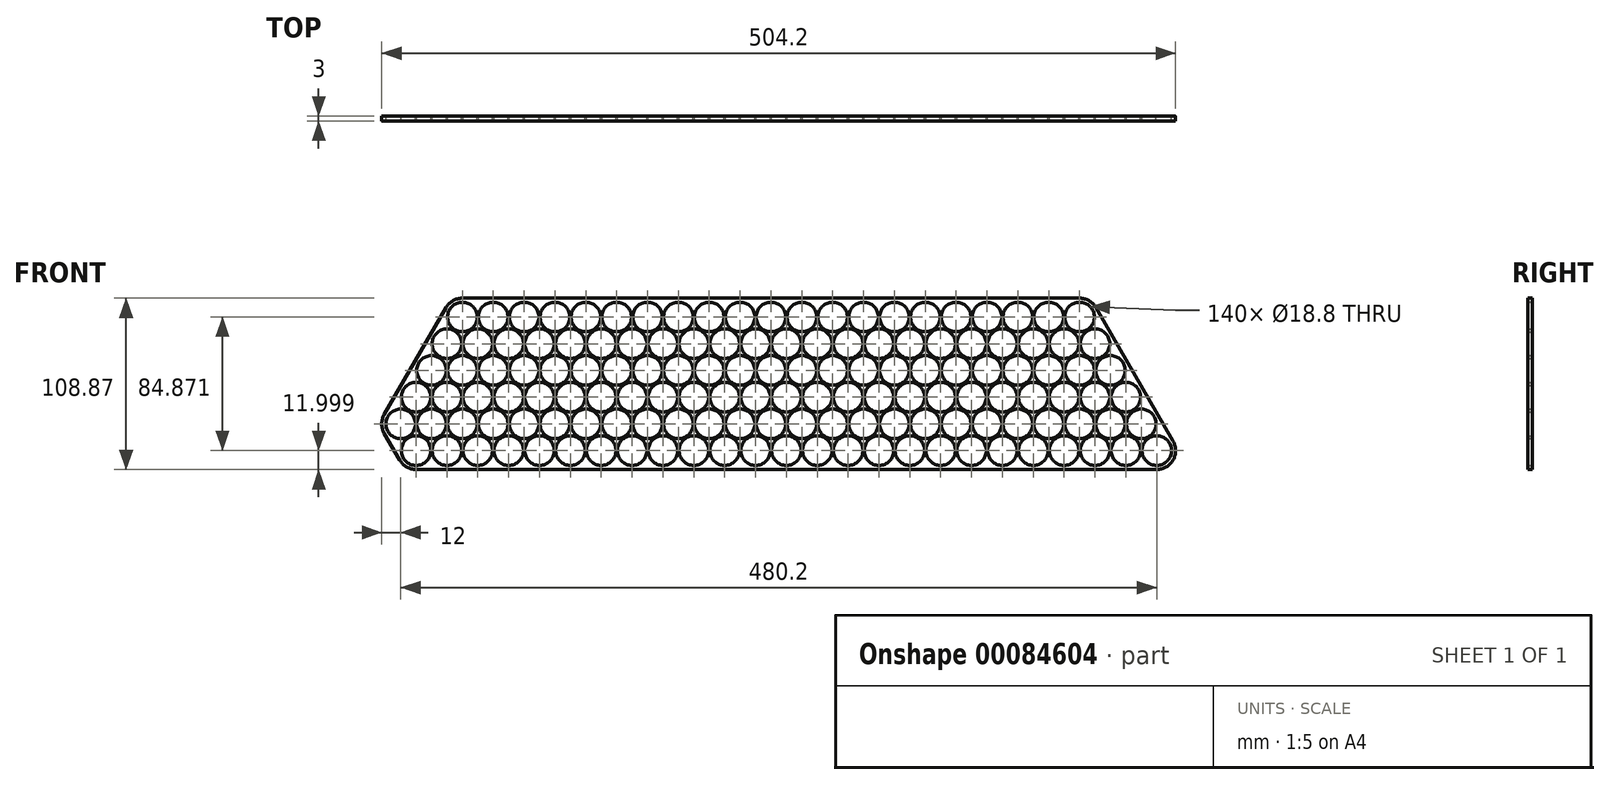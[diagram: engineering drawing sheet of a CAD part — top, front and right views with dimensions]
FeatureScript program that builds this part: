
annotation { "Feature Type Name" : "Feature", "Feature Type Description" : "" }
export const myFeature = defineFeature(function(context is Context, id is Id, definition is map)
    precondition{}
    {
        {
            var Q0;
            Q0=qCreatedBy(makeId("Front.planeOp"),FACE);
            var sketch = newSketch(context, id + "F0", { "sketchPlane" : qUnion([Q0]) });
            skLineSegment(sketch, "E0", {"start": v(0, 0) * mm, "end": v(79.44, 0) * mm, "construction": true});
            skLineSegment(sketch, "E1", {"start": v(0, 0) * mm, "end": v(43.4, -75.16) * mm, "construction": true});
            skCircle(sketch, "E2", {"center": v(0, 0) * mm, "radius": 9.4 * mm});
            skCircle(sketch, "E3.1.0.0", {"center": v(19.6, 0) * mm, "radius": 9.4 * mm});
            skCircle(sketch, "E3.2.0.0", {"center": v(39.2, 0) * mm, "radius": 9.4 * mm});
            skCircle(sketch, "E3.3.0.0", {"center": v(58.8, 0) * mm, "radius": 9.4 * mm});
            skCircle(sketch, "E3.4.0.0", {"center": v(78.4, 0) * mm, "radius": 9.4 * mm});
            skCircle(sketch, "E3.5.0.0", {"center": v(98, 0) * mm, "radius": 9.4 * mm});
            skCircle(sketch, "E3.6.0.0", {"center": v(117.6, 0) * mm, "radius": 9.4 * mm});
            skCircle(sketch, "E3.7.0.0", {"center": v(137.2, 0) * mm, "radius": 9.4 * mm});
            skCircle(sketch, "E3.8.0.0", {"center": v(156.8, 0) * mm, "radius": 9.4 * mm});
            skCircle(sketch, "E3.9.0.0", {"center": v(176.4, 0) * mm, "radius": 9.4 * mm});
            skCircle(sketch, "E3.10.0.0", {"center": v(196, 0) * mm, "radius": 9.4 * mm});
            skCircle(sketch, "E3.11.0.0", {"center": v(215.6, 0) * mm, "radius": 9.4 * mm});
            skCircle(sketch, "E3.12.0.0", {"center": v(235.2, 0) * mm, "radius": 9.4 * mm});
            skCircle(sketch, "E3.13.0.0", {"center": v(254.8, 0) * mm, "radius": 9.4 * mm});
            skCircle(sketch, "E3.14.0.0", {"center": v(274.4, 0) * mm, "radius": 9.4 * mm});
            skCircle(sketch, "E3.15.0.0", {"center": v(294, 0) * mm, "radius": 9.4 * mm});
            skCircle(sketch, "E3.16.0.0", {"center": v(313.6, 0) * mm, "radius": 9.4 * mm});
            skCircle(sketch, "E3.17.0.0", {"center": v(333.2, 0) * mm, "radius": 9.4 * mm});
            skCircle(sketch, "E3.18.0.0", {"center": v(352.8, 0) * mm, "radius": 9.4 * mm});
            skCircle(sketch, "E3.19.0.0", {"center": v(372.4, 0) * mm, "radius": 9.4 * mm});
            skLineSegment(sketch, "E3.direction1", {"start": v(0, 0) * mm, "end": v(19.6, 0) * mm, "construction": true});
            skCircle(sketch, "E4.1.0.0", {"center": v(9.8, -16.97) * mm, "radius": 9.4 * mm});
            skCircle(sketch, "E4.2.0.0", {"center": v(19.6, -33.95) * mm, "radius": 9.4 * mm});
            skCircle(sketch, "E4.3.0.0", {"center": v(29.4, -50.92) * mm, "radius": 9.4 * mm});
            skCircle(sketch, "E4.4.0.0", {"center": v(39.2, -67.9) * mm, "radius": 9.4 * mm});
            skCircle(sketch, "E4.5.0.0", {"center": v(49, -84.87) * mm, "radius": 9.4 * mm});
            skLineSegment(sketch, "E4.direction1", {"start": v(0, 0) * mm, "end": v(9.8, -16.97) * mm, "construction": true});
            skCircle(sketch, "E5.1.0.0", {"center": v(29.4, -16.97) * mm, "radius": 9.4 * mm});
            skCircle(sketch, "E5.1.0.1", {"center": v(39.2, -33.95) * mm, "radius": 9.4 * mm});
            skCircle(sketch, "E5.1.0.2", {"center": v(49, -50.92) * mm, "radius": 9.4 * mm});
            skCircle(sketch, "E5.1.0.3", {"center": v(58.8, -67.9) * mm, "radius": 9.4 * mm});
            skCircle(sketch, "E5.1.0.4", {"center": v(68.6, -84.87) * mm, "radius": 9.4 * mm});
            skCircle(sketch, "E5.2.0.0", {"center": v(49, -16.97) * mm, "radius": 9.4 * mm});
            skCircle(sketch, "E5.2.0.1", {"center": v(58.8, -33.95) * mm, "radius": 9.4 * mm});
            skCircle(sketch, "E5.2.0.2", {"center": v(68.6, -50.92) * mm, "radius": 9.4 * mm});
            skCircle(sketch, "E5.2.0.3", {"center": v(78.4, -67.9) * mm, "radius": 9.4 * mm});
            skCircle(sketch, "E5.2.0.4", {"center": v(88.2, -84.87) * mm, "radius": 9.4 * mm});
            skCircle(sketch, "E5.3.0.0", {"center": v(68.6, -16.97) * mm, "radius": 9.4 * mm});
            skCircle(sketch, "E5.3.0.1", {"center": v(78.4, -33.95) * mm, "radius": 9.4 * mm});
            skCircle(sketch, "E5.3.0.2", {"center": v(88.2, -50.92) * mm, "radius": 9.4 * mm});
            skCircle(sketch, "E5.3.0.3", {"center": v(98, -67.9) * mm, "radius": 9.4 * mm});
            skCircle(sketch, "E5.3.0.4", {"center": v(107.8, -84.87) * mm, "radius": 9.4 * mm});
            skCircle(sketch, "E5.4.0.0", {"center": v(88.2, -16.97) * mm, "radius": 9.4 * mm});
            skCircle(sketch, "E5.4.0.1", {"center": v(98, -33.95) * mm, "radius": 9.4 * mm});
            skCircle(sketch, "E5.4.0.2", {"center": v(107.8, -50.92) * mm, "radius": 9.4 * mm});
            skCircle(sketch, "E5.4.0.3", {"center": v(117.6, -67.9) * mm, "radius": 9.4 * mm});
            skCircle(sketch, "E5.4.0.4", {"center": v(127.4, -84.87) * mm, "radius": 9.4 * mm});
            skCircle(sketch, "E5.5.0.0", {"center": v(107.8, -16.97) * mm, "radius": 9.4 * mm});
            skCircle(sketch, "E5.5.0.1", {"center": v(117.6, -33.95) * mm, "radius": 9.4 * mm});
            skCircle(sketch, "E5.5.0.2", {"center": v(127.4, -50.92) * mm, "radius": 9.4 * mm});
            skCircle(sketch, "E5.5.0.3", {"center": v(137.2, -67.9) * mm, "radius": 9.4 * mm});
            skCircle(sketch, "E5.5.0.4", {"center": v(147, -84.87) * mm, "radius": 9.4 * mm});
            skCircle(sketch, "E5.6.0.0", {"center": v(127.4, -16.97) * mm, "radius": 9.4 * mm});
            skCircle(sketch, "E5.6.0.1", {"center": v(137.2, -33.95) * mm, "radius": 9.4 * mm});
            skCircle(sketch, "E5.6.0.2", {"center": v(147, -50.92) * mm, "radius": 9.4 * mm});
            skCircle(sketch, "E5.6.0.3", {"center": v(156.8, -67.9) * mm, "radius": 9.4 * mm});
            skCircle(sketch, "E5.6.0.4", {"center": v(166.6, -84.87) * mm, "radius": 9.4 * mm});
            skCircle(sketch, "E5.7.0.0", {"center": v(147, -16.97) * mm, "radius": 9.4 * mm});
            skCircle(sketch, "E5.7.0.1", {"center": v(156.8, -33.95) * mm, "radius": 9.4 * mm});
            skCircle(sketch, "E5.7.0.2", {"center": v(166.6, -50.92) * mm, "radius": 9.4 * mm});
            skCircle(sketch, "E5.7.0.3", {"center": v(176.4, -67.9) * mm, "radius": 9.4 * mm});
            skCircle(sketch, "E5.7.0.4", {"center": v(186.2, -84.87) * mm, "radius": 9.4 * mm});
            skCircle(sketch, "E5.8.0.0", {"center": v(166.6, -16.97) * mm, "radius": 9.4 * mm});
            skCircle(sketch, "E5.8.0.1", {"center": v(176.4, -33.95) * mm, "radius": 9.4 * mm});
            skCircle(sketch, "E5.8.0.2", {"center": v(186.2, -50.92) * mm, "radius": 9.4 * mm});
            skCircle(sketch, "E5.8.0.3", {"center": v(196, -67.9) * mm, "radius": 9.4 * mm});
            skCircle(sketch, "E5.8.0.4", {"center": v(205.8, -84.87) * mm, "radius": 9.4 * mm});
            skCircle(sketch, "E5.9.0.0", {"center": v(186.2, -16.97) * mm, "radius": 9.4 * mm});
            skCircle(sketch, "E5.9.0.1", {"center": v(196, -33.95) * mm, "radius": 9.4 * mm});
            skCircle(sketch, "E5.9.0.2", {"center": v(205.8, -50.92) * mm, "radius": 9.4 * mm});
            skCircle(sketch, "E5.9.0.3", {"center": v(215.6, -67.9) * mm, "radius": 9.4 * mm});
            skCircle(sketch, "E5.9.0.4", {"center": v(225.4, -84.87) * mm, "radius": 9.4 * mm});
            skCircle(sketch, "E5.10.0.0", {"center": v(205.8, -16.97) * mm, "radius": 9.4 * mm});
            skCircle(sketch, "E5.10.0.1", {"center": v(215.6, -33.95) * mm, "radius": 9.4 * mm});
            skCircle(sketch, "E5.10.0.2", {"center": v(225.4, -50.92) * mm, "radius": 9.4 * mm});
            skCircle(sketch, "E5.10.0.3", {"center": v(235.2, -67.9) * mm, "radius": 9.4 * mm});
            skCircle(sketch, "E5.10.0.4", {"center": v(245, -84.87) * mm, "radius": 9.4 * mm});
            skCircle(sketch, "E5.11.0.0", {"center": v(225.4, -16.97) * mm, "radius": 9.4 * mm});
            skCircle(sketch, "E5.11.0.1", {"center": v(235.2, -33.95) * mm, "radius": 9.4 * mm});
            skCircle(sketch, "E5.11.0.2", {"center": v(245, -50.92) * mm, "radius": 9.4 * mm});
            skCircle(sketch, "E5.11.0.3", {"center": v(254.8, -67.9) * mm, "radius": 9.4 * mm});
            skCircle(sketch, "E5.11.0.4", {"center": v(264.6, -84.87) * mm, "radius": 9.4 * mm});
            skCircle(sketch, "E5.12.0.0", {"center": v(245, -16.97) * mm, "radius": 9.4 * mm});
            skCircle(sketch, "E5.12.0.1", {"center": v(254.8, -33.95) * mm, "radius": 9.4 * mm});
            skCircle(sketch, "E5.12.0.2", {"center": v(264.6, -50.92) * mm, "radius": 9.4 * mm});
            skCircle(sketch, "E5.12.0.3", {"center": v(274.4, -67.9) * mm, "radius": 9.4 * mm});
            skCircle(sketch, "E5.12.0.4", {"center": v(284.2, -84.87) * mm, "radius": 9.4 * mm});
            skCircle(sketch, "E5.13.0.0", {"center": v(264.6, -16.97) * mm, "radius": 9.4 * mm});
            skCircle(sketch, "E5.13.0.1", {"center": v(274.4, -33.95) * mm, "radius": 9.4 * mm});
            skCircle(sketch, "E5.13.0.2", {"center": v(284.2, -50.92) * mm, "radius": 9.4 * mm});
            skCircle(sketch, "E5.13.0.3", {"center": v(294, -67.9) * mm, "radius": 9.4 * mm});
            skCircle(sketch, "E5.13.0.4", {"center": v(303.8, -84.87) * mm, "radius": 9.4 * mm});
            skCircle(sketch, "E5.14.0.0", {"center": v(284.2, -16.97) * mm, "radius": 9.4 * mm});
            skCircle(sketch, "E5.14.0.1", {"center": v(294, -33.95) * mm, "radius": 9.4 * mm});
            skCircle(sketch, "E5.14.0.2", {"center": v(303.8, -50.92) * mm, "radius": 9.4 * mm});
            skCircle(sketch, "E5.14.0.3", {"center": v(313.6, -67.9) * mm, "radius": 9.4 * mm});
            skCircle(sketch, "E5.14.0.4", {"center": v(323.4, -84.87) * mm, "radius": 9.4 * mm});
            skCircle(sketch, "E5.15.0.0", {"center": v(303.8, -16.97) * mm, "radius": 9.4 * mm});
            skCircle(sketch, "E5.15.0.1", {"center": v(313.6, -33.95) * mm, "radius": 9.4 * mm});
            skCircle(sketch, "E5.15.0.2", {"center": v(323.4, -50.92) * mm, "radius": 9.4 * mm});
            skCircle(sketch, "E5.15.0.3", {"center": v(333.2, -67.9) * mm, "radius": 9.4 * mm});
            skCircle(sketch, "E5.15.0.4", {"center": v(343, -84.87) * mm, "radius": 9.4 * mm});
            skCircle(sketch, "E5.16.0.0", {"center": v(323.4, -16.97) * mm, "radius": 9.4 * mm});
            skCircle(sketch, "E5.16.0.1", {"center": v(333.2, -33.95) * mm, "radius": 9.4 * mm});
            skCircle(sketch, "E5.16.0.2", {"center": v(343, -50.92) * mm, "radius": 9.4 * mm});
            skCircle(sketch, "E5.16.0.3", {"center": v(352.8, -67.9) * mm, "radius": 9.4 * mm});
            skCircle(sketch, "E5.16.0.4", {"center": v(362.6, -84.87) * mm, "radius": 9.4 * mm});
            skCircle(sketch, "E5.17.0.0", {"center": v(343, -16.97) * mm, "radius": 9.4 * mm});
            skCircle(sketch, "E5.17.0.1", {"center": v(352.8, -33.95) * mm, "radius": 9.4 * mm});
            skCircle(sketch, "E5.17.0.2", {"center": v(362.6, -50.92) * mm, "radius": 9.4 * mm});
            skCircle(sketch, "E5.17.0.3", {"center": v(372.4, -67.9) * mm, "radius": 9.4 * mm});
            skCircle(sketch, "E5.17.0.4", {"center": v(382.2, -84.87) * mm, "radius": 9.4 * mm});
            skCircle(sketch, "E5.18.0.0", {"center": v(362.6, -16.97) * mm, "radius": 9.4 * mm});
            skCircle(sketch, "E5.18.0.1", {"center": v(372.4, -33.95) * mm, "radius": 9.4 * mm});
            skCircle(sketch, "E5.18.0.2", {"center": v(382.2, -50.92) * mm, "radius": 9.4 * mm});
            skCircle(sketch, "E5.18.0.3", {"center": v(392, -67.9) * mm, "radius": 9.4 * mm});
            skCircle(sketch, "E5.18.0.4", {"center": v(401.8, -84.87) * mm, "radius": 9.4 * mm});
            skCircle(sketch, "E5.19.0.0", {"center": v(382.2, -16.97) * mm, "radius": 9.4 * mm});
            skCircle(sketch, "E5.19.0.1", {"center": v(392, -33.95) * mm, "radius": 9.4 * mm});
            skCircle(sketch, "E5.19.0.2", {"center": v(401.8, -50.92) * mm, "radius": 9.4 * mm});
            skCircle(sketch, "E5.19.0.3", {"center": v(411.6, -67.9) * mm, "radius": 9.4 * mm});
            skCircle(sketch, "E5.19.0.4", {"center": v(421.4, -84.87) * mm, "radius": 9.4 * mm});
            skLineSegment(sketch, "E5.direction1", {"start": v(9.8, -16.97) * mm, "end": v(29.4, -16.97) * mm, "construction": true});
            skLineSegment(sketch, "E6", {"start": v(0, 0) * mm, "end": v(372.4, 0) * mm, "construction": true});
            skLineSegment(sketch, "E7", {"start": v(372.4, 0) * mm, "end": v(421.4, -84.87) * mm, "construction": true});
            skLineSegment(sketch, "E8", {"start": v(49, -84.87) * mm, "end": v(0, 0) * mm, "construction": true});
            skLineSegment(sketch, "E9.0", {"start": v(-20.78, 12) * mm, "end": v(372.4, 12) * mm});
            skLineSegment(sketch, "E9.1", {"start": v(42.07, -96.87) * mm, "end": v(-20.78, 12) * mm, "construction": true});
            skLineSegment(sketch, "E10", {"start": v(49, -84.87) * mm, "end": v(421.4, -84.87) * mm, "construction": true});
            skLineSegment(sketch, "E11.0", {"start": v(49, -96.87) * mm, "end": v(421.4, -96.87) * mm});
            skLineSegment(sketch, "E12", {"start": v(49, -96.87) * mm, "end": v(42.07, -96.87) * mm});
            skLineSegment(sketch, "E13", {"start": v(42.07, -96.87) * mm, "end": v(-49, -96.87) * mm});
            skPoint(sketch, "E13.endSnap0", {"position": v(45.54, -96.87) * mm});
            skLineSegment(sketch, "E14", {"start": v(-20.78, 12) * mm, "end": v(-20.84, 11.94) * mm});
            skCircle(sketch, "E15.1.0.0", {"center": v(29.4, -84.87) * mm, "radius": 9.4 * mm});
            skCircle(sketch, "E15.2.0.0", {"center": v(9.8, -84.87) * mm, "radius": 9.4 * mm});
            skCircle(sketch, "E15.3.0.0", {"center": v(-9.8, -84.87) * mm, "radius": 9.4 * mm});
            skCircle(sketch, "E15.4.0.0", {"center": v(-29.4, -84.87) * mm, "radius": 9.4 * mm});
            skCircle(sketch, "E15.5.0.0", {"center": v(-49, -84.87) * mm, "radius": 9.4 * mm});
            skLineSegment(sketch, "E15.direction1", {"start": v(49, -84.87) * mm, "end": v(29.4, -84.87) * mm, "construction": true});
            skCircle(sketch, "E16.1.0.0", {"center": v(19.6, -67.9) * mm, "radius": 9.4 * mm});
            skCircle(sketch, "E16.2.0.0", {"center": v(0, -67.9) * mm, "radius": 9.4 * mm});
            skCircle(sketch, "E16.3.0.0", {"center": v(-19.6, -67.9) * mm, "radius": 9.4 * mm});
            skCircle(sketch, "E16.4.0.0", {"center": v(-39.2, -67.9) * mm, "radius": 9.4 * mm});
            skCircle(sketch, "E16.5.0.0", {"center": v(-58.8, -67.9) * mm, "radius": 9.4 * mm});
            skLineSegment(sketch, "E16.direction1", {"start": v(39.2, -67.9) * mm, "end": v(19.6, -67.9) * mm, "construction": true});
            skCircle(sketch, "E17.1.0.0", {"center": v(9.8, -50.92) * mm, "radius": 9.4 * mm});
            skCircle(sketch, "E17.2.0.0", {"center": v(-9.8, -50.92) * mm, "radius": 9.4 * mm});
            skCircle(sketch, "E17.3.0.0", {"center": v(-29.4, -50.92) * mm, "radius": 9.4 * mm});
            skCircle(sketch, "E17.4.0.0", {"center": v(-49, -50.92) * mm, "radius": 9.4 * mm});
            skLineSegment(sketch, "E17.direction1", {"start": v(29.4, -50.92) * mm, "end": v(9.8, -50.92) * mm, "construction": true});
            skCircle(sketch, "E18.1.0.0", {"center": v(0, -33.95) * mm, "radius": 9.4 * mm});
            skCircle(sketch, "E18.2.0.0", {"center": v(-19.6, -33.95) * mm, "radius": 9.4 * mm});
            skCircle(sketch, "E18.3.0.0", {"center": v(-39.2, -33.95) * mm, "radius": 9.4 * mm});
            skLineSegment(sketch, "E18.direction1", {"start": v(19.6, -33.95) * mm, "end": v(0, -33.95) * mm, "construction": true});
            skCircle(sketch, "E19.1.0.0", {"center": v(-9.8, -16.97) * mm, "radius": 9.4 * mm});
            skCircle(sketch, "E19.2.0.0", {"center": v(-29.4, -16.97) * mm, "radius": 9.4 * mm});
            skLineSegment(sketch, "E19.direction1", {"start": v(9.8, -16.97) * mm, "end": v(-9.8, -16.97) * mm, "construction": true});
            skCircle(sketch, "E20.1.0.0", {"center": v(-19.6, 0) * mm, "radius": 9.4 * mm});
            skLineSegment(sketch, "E20.direction1", {"start": v(0, 0) * mm, "end": v(-19.6, 0) * mm, "construction": true});
            skArc(sketch, "E21.0", {"start": v(-19.6, 12) * mm, "mid": v(-25.6, 10.4) * mm, "end": v(-30, 6) * mm});
            skLineSegment(sketch, "E22", {"start": v(-30, 6) * mm, "end": v(-69.2, -61.9) * mm});
            skPoint(sketch, "E23.orphan", {"position": v(-115.18, -96.87) * mm});
            skArc(sketch, "E24.trimOffspring", {"start": v(-69.2, -61.9) * mm, "mid": v(-70.8, -67.9) * mm, "end": v(-69.2, -73.9) * mm});
            skLineSegment(sketch, "E25", {"start": v(-59.4, -90.87) * mm, "end": v(-69.2, -73.9) * mm});
            skArc(sketch, "E26.trimOffspring", {"start": v(-59.4, -90.87) * mm, "mid": v(-55, -95.26) * mm, "end": v(-49, -96.87) * mm});
            skArc(sketch, "E27", {"start": v(421.4, -96.87) * mm, "mid": v(431.8, -90.87) * mm, "end": v(431.8, -78.87) * mm});
            skArc(sketch, "E28", {"start": v(382.8, 6) * mm, "mid": v(378.4, 10.4) * mm, "end": v(372.4, 12) * mm});
            skLineSegment(sketch, "E29", {"start": v(431.8, -78.87) * mm, "end": v(382.8, 6) * mm});
            skSolve(sketch);
        }
        {
            var Q0;
            Q0=makeQuery(id+"F0.imprint","IMPRINT",FACE,{"disambiguationData":[TD([[makeQuery(id+"F0.imprint","IMPRINT",EDGE,{"derivedFrom":sQuery(id+"F0.wireOp",EDGE,"E2")}),-1.0]])]});
            extrude(context, id + "F1", {"entities" : qUnion([Q0]), "depth" : 3 * mm});
        }
        {
            var Q0;
            Q0=makeQuery(id+"F0.imprint","IMPRINT",FACE,{"disambiguationData":[TD([[makeQuery(id+"F0.imprint","IMPRINT",EDGE,{"derivedFrom":sQuery(id+"F0.wireOp",EDGE,"E2")}),-1.0]])]});
            var Q1;
            Q1=makeQuery(id+"F0.imprint","IMPRINT",FACE,{"disambiguationData":[TD([[makeQuery(id+"F0.imprint","IMPRINT",EDGE,{"derivedFrom":sQuery(id+"F0.wireOp",EDGE,"E3.19.0.0")}),1.0]])]});
            var Q2;
            Q2=makeQuery(id+"F0.imprint","IMPRINT",FACE,{"disambiguationData":[TD([[makeQuery(id+"F0.imprint","IMPRINT",EDGE,{"derivedFrom":sQuery(id+"F0.wireOp",EDGE,"E3.18.0.0")}),1.0]])]});
            var Q3;
            Q3=makeQuery(id+"F0.imprint","IMPRINT",FACE,{"disambiguationData":[TD([[makeQuery(id+"F0.imprint","IMPRINT",EDGE,{"derivedFrom":sQuery(id+"F0.wireOp",EDGE,"E3.17.0.0")}),1.0]])]});
            var Q4;
            Q4=makeQuery(id+"F0.imprint","IMPRINT",FACE,{"disambiguationData":[TD([[makeQuery(id+"F0.imprint","IMPRINT",EDGE,{"derivedFrom":sQuery(id+"F0.wireOp",EDGE,"E3.16.0.0")}),1.0]])]});
            var Q5;
            Q5=makeQuery(id+"F0.imprint","IMPRINT",FACE,{"disambiguationData":[TD([[makeQuery(id+"F0.imprint","IMPRINT",EDGE,{"derivedFrom":sQuery(id+"F0.wireOp",EDGE,"E3.15.0.0")}),1.0]])]});
            var Q6;
            Q6=makeQuery(id+"F0.imprint","IMPRINT",FACE,{"disambiguationData":[TD([[makeQuery(id+"F0.imprint","IMPRINT",EDGE,{"derivedFrom":sQuery(id+"F0.wireOp",EDGE,"E3.14.0.0")}),1.0]])]});
            var Q7;
            Q7=makeQuery(id+"F0.imprint","IMPRINT",FACE,{"disambiguationData":[TD([[makeQuery(id+"F0.imprint","IMPRINT",EDGE,{"derivedFrom":sQuery(id+"F0.wireOp",EDGE,"E3.13.0.0")}),1.0]])]});
            var Q8;
            Q8=makeQuery(id+"F0.imprint","IMPRINT",FACE,{"disambiguationData":[TD([[makeQuery(id+"F0.imprint","IMPRINT",EDGE,{"derivedFrom":sQuery(id+"F0.wireOp",EDGE,"E3.12.0.0")}),1.0]])]});
            var Q9;
            Q9=makeQuery(id+"F0.imprint","IMPRINT",FACE,{"disambiguationData":[TD([[makeQuery(id+"F0.imprint","IMPRINT",EDGE,{"derivedFrom":sQuery(id+"F0.wireOp",EDGE,"E3.11.0.0")}),1.0]])]});
            var Q10;
            Q10=makeQuery(id+"F0.imprint","IMPRINT",FACE,{"disambiguationData":[TD([[makeQuery(id+"F0.imprint","IMPRINT",EDGE,{"derivedFrom":sQuery(id+"F0.wireOp",EDGE,"E3.10.0.0")}),1.0]])]});
            var Q11;
            Q11=makeQuery(id+"F0.imprint","IMPRINT",FACE,{"disambiguationData":[TD([[makeQuery(id+"F0.imprint","IMPRINT",EDGE,{"derivedFrom":sQuery(id+"F0.wireOp",EDGE,"E3.9.0.0")}),1.0]])]});
            var Q12;
            Q12=makeQuery(id+"F0.imprint","IMPRINT",FACE,{"disambiguationData":[TD([[makeQuery(id+"F0.imprint","IMPRINT",EDGE,{"derivedFrom":sQuery(id+"F0.wireOp",EDGE,"E3.8.0.0")}),1.0]])]});
            var Q13;
            Q13=makeQuery(id+"F0.imprint","IMPRINT",FACE,{"disambiguationData":[TD([[makeQuery(id+"F0.imprint","IMPRINT",EDGE,{"derivedFrom":sQuery(id+"F0.wireOp",EDGE,"E3.7.0.0")}),1.0]])]});
            var Q14;
            Q14=makeQuery(id+"F0.imprint","IMPRINT",FACE,{"disambiguationData":[TD([[makeQuery(id+"F0.imprint","IMPRINT",EDGE,{"derivedFrom":sQuery(id+"F0.wireOp",EDGE,"E3.6.0.0")}),1.0]])]});
            var Q15;
            Q15=makeQuery(id+"F0.imprint","IMPRINT",FACE,{"disambiguationData":[TD([[makeQuery(id+"F0.imprint","IMPRINT",EDGE,{"derivedFrom":sQuery(id+"F0.wireOp",EDGE,"E3.5.0.0")}),1.0]])]});
            var Q16;
            Q16=makeQuery(id+"F0.imprint","IMPRINT",FACE,{"disambiguationData":[TD([[makeQuery(id+"F0.imprint","IMPRINT",EDGE,{"derivedFrom":sQuery(id+"F0.wireOp",EDGE,"E3.4.0.0")}),1.0]])]});
            var Q17;
            Q17=makeQuery(id+"F0.imprint","IMPRINT",FACE,{"disambiguationData":[TD([[makeQuery(id+"F0.imprint","IMPRINT",EDGE,{"derivedFrom":sQuery(id+"F0.wireOp",EDGE,"E3.3.0.0")}),1.0]])]});
            var Q18;
            Q18=makeQuery(id+"F0.imprint","IMPRINT",FACE,{"disambiguationData":[TD([[makeQuery(id+"F0.imprint","IMPRINT",EDGE,{"derivedFrom":sQuery(id+"F0.wireOp",EDGE,"E3.2.0.0")}),1.0]])]});
            var Q19;
            Q19=makeQuery(id+"F0.imprint","IMPRINT",FACE,{"disambiguationData":[TD([[makeQuery(id+"F0.imprint","IMPRINT",EDGE,{"derivedFrom":sQuery(id+"F0.wireOp",EDGE,"E3.1.0.0")}),1.0]])]});
            var Q20;
            Q20=makeQuery(id+"F0.imprint","IMPRINT",FACE,{"disambiguationData":[TD([[makeQuery(id+"F0.imprint","IMPRINT",EDGE,{"derivedFrom":sQuery(id+"F0.wireOp",EDGE,"E2")}),1.0]])]});
            var Q21;
            Q21=makeQuery(id+"F0.imprint","IMPRINT",FACE,{"disambiguationData":[TD([[makeQuery(id+"F0.imprint","IMPRINT",EDGE,{"derivedFrom":sQuery(id+"F0.wireOp",EDGE,"E20.1.0.0")}),1.0]])]});
            var Q22;
            Q22=makeQuery(id+"F0.imprint","IMPRINT",FACE,{"disambiguationData":[TD([[makeQuery(id+"F0.imprint","IMPRINT",EDGE,{"derivedFrom":sQuery(id+"F0.wireOp",EDGE,"E19.2.0.0")}),1.0]])]});
            var Q23;
            Q23=makeQuery(id+"F0.imprint","IMPRINT",FACE,{"disambiguationData":[TD([[makeQuery(id+"F0.imprint","IMPRINT",EDGE,{"derivedFrom":sQuery(id+"F0.wireOp",EDGE,"E19.1.0.0")}),1.0]])]});
            var Q24;
            Q24=makeQuery(id+"F0.imprint","IMPRINT",FACE,{"disambiguationData":[TD([[makeQuery(id+"F0.imprint","IMPRINT",EDGE,{"derivedFrom":sQuery(id+"F0.wireOp",EDGE,"E4.1.0.0")}),1.0]])]});
            var Q25;
            Q25=makeQuery(id+"F0.imprint","IMPRINT",FACE,{"disambiguationData":[TD([[makeQuery(id+"F0.imprint","IMPRINT",EDGE,{"derivedFrom":sQuery(id+"F0.wireOp",EDGE,"E5.1.0.0")}),1.0]])]});
            var Q26;
            Q26=makeQuery(id+"F0.imprint","IMPRINT",FACE,{"disambiguationData":[TD([[makeQuery(id+"F0.imprint","IMPRINT",EDGE,{"derivedFrom":sQuery(id+"F0.wireOp",EDGE,"E5.2.0.0")}),1.0]])]});
            var Q27;
            Q27=makeQuery(id+"F0.imprint","IMPRINT",FACE,{"disambiguationData":[TD([[makeQuery(id+"F0.imprint","IMPRINT",EDGE,{"derivedFrom":sQuery(id+"F0.wireOp",EDGE,"E5.3.0.0")}),1.0]])]});
            var Q28;
            Q28=makeQuery(id+"F0.imprint","IMPRINT",FACE,{"disambiguationData":[TD([[makeQuery(id+"F0.imprint","IMPRINT",EDGE,{"derivedFrom":sQuery(id+"F0.wireOp",EDGE,"E5.4.0.0")}),1.0]])]});
            var Q29;
            Q29=makeQuery(id+"F0.imprint","IMPRINT",FACE,{"disambiguationData":[TD([[makeQuery(id+"F0.imprint","IMPRINT",EDGE,{"derivedFrom":sQuery(id+"F0.wireOp",EDGE,"E5.5.0.0")}),1.0]])]});
            var Q30;
            Q30=makeQuery(id+"F0.imprint","IMPRINT",FACE,{"disambiguationData":[TD([[makeQuery(id+"F0.imprint","IMPRINT",EDGE,{"derivedFrom":sQuery(id+"F0.wireOp",EDGE,"E5.6.0.0")}),1.0]])]});
            var Q31;
            Q31=makeQuery(id+"F0.imprint","IMPRINT",FACE,{"disambiguationData":[TD([[makeQuery(id+"F0.imprint","IMPRINT",EDGE,{"derivedFrom":sQuery(id+"F0.wireOp",EDGE,"E5.7.0.0")}),1.0]])]});
            var Q32;
            Q32=makeQuery(id+"F0.imprint","IMPRINT",FACE,{"disambiguationData":[TD([[makeQuery(id+"F0.imprint","IMPRINT",EDGE,{"derivedFrom":sQuery(id+"F0.wireOp",EDGE,"E5.8.0.0")}),1.0]])]});
            var Q33;
            Q33=makeQuery(id+"F0.imprint","IMPRINT",FACE,{"disambiguationData":[TD([[makeQuery(id+"F0.imprint","IMPRINT",EDGE,{"derivedFrom":sQuery(id+"F0.wireOp",EDGE,"E5.9.0.0")}),1.0]])]});
            var Q34;
            Q34=makeQuery(id+"F0.imprint","IMPRINT",FACE,{"disambiguationData":[TD([[makeQuery(id+"F0.imprint","IMPRINT",EDGE,{"derivedFrom":sQuery(id+"F0.wireOp",EDGE,"E5.10.0.0")}),1.0]])]});
            var Q35;
            Q35=makeQuery(id+"F0.imprint","IMPRINT",FACE,{"disambiguationData":[TD([[makeQuery(id+"F0.imprint","IMPRINT",EDGE,{"derivedFrom":sQuery(id+"F0.wireOp",EDGE,"E5.11.0.0")}),1.0]])]});
            var Q36;
            Q36=makeQuery(id+"F0.imprint","IMPRINT",FACE,{"disambiguationData":[TD([[makeQuery(id+"F0.imprint","IMPRINT",EDGE,{"derivedFrom":sQuery(id+"F0.wireOp",EDGE,"E5.12.0.0")}),1.0]])]});
            var Q37;
            Q37=makeQuery(id+"F0.imprint","IMPRINT",FACE,{"disambiguationData":[TD([[makeQuery(id+"F0.imprint","IMPRINT",EDGE,{"derivedFrom":sQuery(id+"F0.wireOp",EDGE,"E5.13.0.0")}),1.0]])]});
            var Q38;
            Q38=makeQuery(id+"F0.imprint","IMPRINT",FACE,{"disambiguationData":[TD([[makeQuery(id+"F0.imprint","IMPRINT",EDGE,{"derivedFrom":sQuery(id+"F0.wireOp",EDGE,"E5.14.0.0")}),1.0]])]});
            var Q39;
            Q39=makeQuery(id+"F0.imprint","IMPRINT",FACE,{"disambiguationData":[TD([[makeQuery(id+"F0.imprint","IMPRINT",EDGE,{"derivedFrom":sQuery(id+"F0.wireOp",EDGE,"E5.15.0.0")}),1.0]])]});
            var Q40;
            Q40=makeQuery(id+"F0.imprint","IMPRINT",FACE,{"disambiguationData":[TD([[makeQuery(id+"F0.imprint","IMPRINT",EDGE,{"derivedFrom":sQuery(id+"F0.wireOp",EDGE,"E5.16.0.0")}),1.0]])]});
            var Q41;
            Q41=makeQuery(id+"F0.imprint","IMPRINT",FACE,{"disambiguationData":[TD([[makeQuery(id+"F0.imprint","IMPRINT",EDGE,{"derivedFrom":sQuery(id+"F0.wireOp",EDGE,"E5.17.0.0")}),1.0]])]});
            var Q42;
            Q42=makeQuery(id+"F0.imprint","IMPRINT",FACE,{"disambiguationData":[TD([[makeQuery(id+"F0.imprint","IMPRINT",EDGE,{"derivedFrom":sQuery(id+"F0.wireOp",EDGE,"E5.18.0.0")}),1.0]])]});
            var Q43;
            Q43=makeQuery(id+"F0.imprint","IMPRINT",FACE,{"disambiguationData":[TD([[makeQuery(id+"F0.imprint","IMPRINT",EDGE,{"derivedFrom":sQuery(id+"F0.wireOp",EDGE,"E5.19.0.0")}),1.0]])]});
            var Q44;
            Q44=makeQuery(id+"F0.imprint","IMPRINT",FACE,{"disambiguationData":[TD([[makeQuery(id+"F0.imprint","IMPRINT",EDGE,{"derivedFrom":sQuery(id+"F0.wireOp",EDGE,"E5.19.0.1")}),1.0]])]});
            var Q45;
            Q45=makeQuery(id+"F0.imprint","IMPRINT",FACE,{"disambiguationData":[TD([[makeQuery(id+"F0.imprint","IMPRINT",EDGE,{"derivedFrom":sQuery(id+"F0.wireOp",EDGE,"E5.18.0.1")}),1.0]])]});
            var Q46;
            Q46=makeQuery(id+"F0.imprint","IMPRINT",FACE,{"disambiguationData":[TD([[makeQuery(id+"F0.imprint","IMPRINT",EDGE,{"derivedFrom":sQuery(id+"F0.wireOp",EDGE,"E5.17.0.1")}),1.0]])]});
            var Q47;
            Q47=makeQuery(id+"F0.imprint","IMPRINT",FACE,{"disambiguationData":[TD([[makeQuery(id+"F0.imprint","IMPRINT",EDGE,{"derivedFrom":sQuery(id+"F0.wireOp",EDGE,"E5.16.0.1")}),1.0]])]});
            var Q48;
            Q48=makeQuery(id+"F0.imprint","IMPRINT",FACE,{"disambiguationData":[TD([[makeQuery(id+"F0.imprint","IMPRINT",EDGE,{"derivedFrom":sQuery(id+"F0.wireOp",EDGE,"E5.15.0.1")}),1.0]])]});
            var Q49;
            Q49=makeQuery(id+"F0.imprint","IMPRINT",FACE,{"disambiguationData":[TD([[makeQuery(id+"F0.imprint","IMPRINT",EDGE,{"derivedFrom":sQuery(id+"F0.wireOp",EDGE,"E5.14.0.1")}),1.0]])]});
            var Q50;
            Q50=makeQuery(id+"F0.imprint","IMPRINT",FACE,{"disambiguationData":[TD([[makeQuery(id+"F0.imprint","IMPRINT",EDGE,{"derivedFrom":sQuery(id+"F0.wireOp",EDGE,"E5.13.0.1")}),1.0]])]});
            var Q51;
            Q51=makeQuery(id+"F0.imprint","IMPRINT",FACE,{"disambiguationData":[TD([[makeQuery(id+"F0.imprint","IMPRINT",EDGE,{"derivedFrom":sQuery(id+"F0.wireOp",EDGE,"E5.12.0.1")}),1.0]])]});
            var Q52;
            Q52=makeQuery(id+"F0.imprint","IMPRINT",FACE,{"disambiguationData":[TD([[makeQuery(id+"F0.imprint","IMPRINT",EDGE,{"derivedFrom":sQuery(id+"F0.wireOp",EDGE,"E5.11.0.1")}),1.0]])]});
            var Q53;
            Q53=makeQuery(id+"F0.imprint","IMPRINT",FACE,{"disambiguationData":[TD([[makeQuery(id+"F0.imprint","IMPRINT",EDGE,{"derivedFrom":sQuery(id+"F0.wireOp",EDGE,"E5.10.0.1")}),1.0]])]});
            var Q54;
            Q54=makeQuery(id+"F0.imprint","IMPRINT",FACE,{"disambiguationData":[TD([[makeQuery(id+"F0.imprint","IMPRINT",EDGE,{"derivedFrom":sQuery(id+"F0.wireOp",EDGE,"E5.9.0.1")}),1.0]])]});
            var Q55;
            Q55=makeQuery(id+"F0.imprint","IMPRINT",FACE,{"disambiguationData":[TD([[makeQuery(id+"F0.imprint","IMPRINT",EDGE,{"derivedFrom":sQuery(id+"F0.wireOp",EDGE,"E5.8.0.1")}),1.0]])]});
            var Q56;
            Q56=makeQuery(id+"F0.imprint","IMPRINT",FACE,{"disambiguationData":[TD([[makeQuery(id+"F0.imprint","IMPRINT",EDGE,{"derivedFrom":sQuery(id+"F0.wireOp",EDGE,"E5.7.0.1")}),1.0]])]});
            var Q57;
            Q57=makeQuery(id+"F0.imprint","IMPRINT",FACE,{"disambiguationData":[TD([[makeQuery(id+"F0.imprint","IMPRINT",EDGE,{"derivedFrom":sQuery(id+"F0.wireOp",EDGE,"E5.6.0.1")}),1.0]])]});
            var Q58;
            Q58=makeQuery(id+"F0.imprint","IMPRINT",FACE,{"disambiguationData":[TD([[makeQuery(id+"F0.imprint","IMPRINT",EDGE,{"derivedFrom":sQuery(id+"F0.wireOp",EDGE,"E5.5.0.1")}),1.0]])]});
            var Q59;
            Q59=makeQuery(id+"F0.imprint","IMPRINT",FACE,{"disambiguationData":[TD([[makeQuery(id+"F0.imprint","IMPRINT",EDGE,{"derivedFrom":sQuery(id+"F0.wireOp",EDGE,"E5.4.0.1")}),1.0]])]});
            var Q60;
            Q60=makeQuery(id+"F0.imprint","IMPRINT",FACE,{"disambiguationData":[TD([[makeQuery(id+"F0.imprint","IMPRINT",EDGE,{"derivedFrom":sQuery(id+"F0.wireOp",EDGE,"E5.3.0.1")}),1.0]])]});
            var Q61;
            Q61=makeQuery(id+"F0.imprint","IMPRINT",FACE,{"disambiguationData":[TD([[makeQuery(id+"F0.imprint","IMPRINT",EDGE,{"derivedFrom":sQuery(id+"F0.wireOp",EDGE,"E5.2.0.1")}),1.0]])]});
            var Q62;
            Q62=makeQuery(id+"F0.imprint","IMPRINT",FACE,{"disambiguationData":[TD([[makeQuery(id+"F0.imprint","IMPRINT",EDGE,{"derivedFrom":sQuery(id+"F0.wireOp",EDGE,"E5.1.0.1")}),1.0]])]});
            var Q63;
            Q63=makeQuery(id+"F0.imprint","IMPRINT",FACE,{"disambiguationData":[TD([[makeQuery(id+"F0.imprint","IMPRINT",EDGE,{"derivedFrom":sQuery(id+"F0.wireOp",EDGE,"E4.2.0.0")}),1.0]])]});
            var Q64;
            Q64=makeQuery(id+"F0.imprint","IMPRINT",FACE,{"disambiguationData":[TD([[makeQuery(id+"F0.imprint","IMPRINT",EDGE,{"derivedFrom":sQuery(id+"F0.wireOp",EDGE,"E18.1.0.0")}),1.0]])]});
            var Q65;
            Q65=makeQuery(id+"F0.imprint","IMPRINT",FACE,{"disambiguationData":[TD([[makeQuery(id+"F0.imprint","IMPRINT",EDGE,{"derivedFrom":sQuery(id+"F0.wireOp",EDGE,"E18.2.0.0")}),1.0]])]});
            var Q66;
            Q66=makeQuery(id+"F0.imprint","IMPRINT",FACE,{"disambiguationData":[TD([[makeQuery(id+"F0.imprint","IMPRINT",EDGE,{"derivedFrom":sQuery(id+"F0.wireOp",EDGE,"E18.3.0.0")}),1.0]])]});
            var Q67;
            Q67=makeQuery(id+"F0.imprint","IMPRINT",FACE,{"disambiguationData":[TD([[makeQuery(id+"F0.imprint","IMPRINT",EDGE,{"derivedFrom":sQuery(id+"F0.wireOp",EDGE,"E17.4.0.0")}),1.0]])]});
            var Q68;
            Q68=makeQuery(id+"F0.imprint","IMPRINT",FACE,{"disambiguationData":[TD([[makeQuery(id+"F0.imprint","IMPRINT",EDGE,{"derivedFrom":sQuery(id+"F0.wireOp",EDGE,"E17.3.0.0")}),1.0]])]});
            var Q69;
            Q69=makeQuery(id+"F0.imprint","IMPRINT",FACE,{"disambiguationData":[TD([[makeQuery(id+"F0.imprint","IMPRINT",EDGE,{"derivedFrom":sQuery(id+"F0.wireOp",EDGE,"E17.2.0.0")}),1.0]])]});
            var Q70;
            Q70=makeQuery(id+"F0.imprint","IMPRINT",FACE,{"disambiguationData":[TD([[makeQuery(id+"F0.imprint","IMPRINT",EDGE,{"derivedFrom":sQuery(id+"F0.wireOp",EDGE,"E17.1.0.0")}),1.0]])]});
            var Q71;
            Q71=makeQuery(id+"F0.imprint","IMPRINT",FACE,{"disambiguationData":[TD([[makeQuery(id+"F0.imprint","IMPRINT",EDGE,{"derivedFrom":sQuery(id+"F0.wireOp",EDGE,"E4.3.0.0")}),1.0]])]});
            var Q72;
            Q72=makeQuery(id+"F0.imprint","IMPRINT",FACE,{"disambiguationData":[TD([[makeQuery(id+"F0.imprint","IMPRINT",EDGE,{"derivedFrom":sQuery(id+"F0.wireOp",EDGE,"E5.1.0.2")}),1.0]])]});
            var Q73;
            Q73=makeQuery(id+"F0.imprint","IMPRINT",FACE,{"disambiguationData":[TD([[makeQuery(id+"F0.imprint","IMPRINT",EDGE,{"derivedFrom":sQuery(id+"F0.wireOp",EDGE,"E5.2.0.2")}),1.0]])]});
            var Q74;
            Q74=makeQuery(id+"F0.imprint","IMPRINT",FACE,{"disambiguationData":[TD([[makeQuery(id+"F0.imprint","IMPRINT",EDGE,{"derivedFrom":sQuery(id+"F0.wireOp",EDGE,"E5.3.0.2")}),1.0]])]});
            var Q75;
            Q75=makeQuery(id+"F0.imprint","IMPRINT",FACE,{"disambiguationData":[TD([[makeQuery(id+"F0.imprint","IMPRINT",EDGE,{"derivedFrom":sQuery(id+"F0.wireOp",EDGE,"E5.4.0.2")}),1.0]])]});
            var Q76;
            Q76=makeQuery(id+"F0.imprint","IMPRINT",FACE,{"disambiguationData":[TD([[makeQuery(id+"F0.imprint","IMPRINT",EDGE,{"derivedFrom":sQuery(id+"F0.wireOp",EDGE,"E5.5.0.2")}),1.0]])]});
            var Q77;
            Q77=makeQuery(id+"F0.imprint","IMPRINT",FACE,{"disambiguationData":[TD([[makeQuery(id+"F0.imprint","IMPRINT",EDGE,{"derivedFrom":sQuery(id+"F0.wireOp",EDGE,"E5.6.0.2")}),1.0]])]});
            var Q78;
            Q78=makeQuery(id+"F0.imprint","IMPRINT",FACE,{"disambiguationData":[TD([[makeQuery(id+"F0.imprint","IMPRINT",EDGE,{"derivedFrom":sQuery(id+"F0.wireOp",EDGE,"E5.7.0.2")}),1.0]])]});
            var Q79;
            Q79=makeQuery(id+"F0.imprint","IMPRINT",FACE,{"disambiguationData":[TD([[makeQuery(id+"F0.imprint","IMPRINT",EDGE,{"derivedFrom":sQuery(id+"F0.wireOp",EDGE,"E5.8.0.2")}),1.0]])]});
            var Q80;
            Q80=makeQuery(id+"F0.imprint","IMPRINT",FACE,{"disambiguationData":[TD([[makeQuery(id+"F0.imprint","IMPRINT",EDGE,{"derivedFrom":sQuery(id+"F0.wireOp",EDGE,"E5.9.0.2")}),1.0]])]});
            var Q81;
            Q81=makeQuery(id+"F0.imprint","IMPRINT",FACE,{"disambiguationData":[TD([[makeQuery(id+"F0.imprint","IMPRINT",EDGE,{"derivedFrom":sQuery(id+"F0.wireOp",EDGE,"E5.10.0.2")}),1.0]])]});
            var Q82;
            Q82=makeQuery(id+"F0.imprint","IMPRINT",FACE,{"disambiguationData":[TD([[makeQuery(id+"F0.imprint","IMPRINT",EDGE,{"derivedFrom":sQuery(id+"F0.wireOp",EDGE,"E5.11.0.2")}),1.0]])]});
            var Q83;
            Q83=makeQuery(id+"F0.imprint","IMPRINT",FACE,{"disambiguationData":[TD([[makeQuery(id+"F0.imprint","IMPRINT",EDGE,{"derivedFrom":sQuery(id+"F0.wireOp",EDGE,"E5.12.0.2")}),1.0]])]});
            var Q84;
            Q84=makeQuery(id+"F0.imprint","IMPRINT",FACE,{"disambiguationData":[TD([[makeQuery(id+"F0.imprint","IMPRINT",EDGE,{"derivedFrom":sQuery(id+"F0.wireOp",EDGE,"E5.13.0.2")}),1.0]])]});
            var Q85;
            Q85=makeQuery(id+"F0.imprint","IMPRINT",FACE,{"disambiguationData":[TD([[makeQuery(id+"F0.imprint","IMPRINT",EDGE,{"derivedFrom":sQuery(id+"F0.wireOp",EDGE,"E5.14.0.2")}),1.0]])]});
            var Q86;
            Q86=makeQuery(id+"F0.imprint","IMPRINT",FACE,{"disambiguationData":[TD([[makeQuery(id+"F0.imprint","IMPRINT",EDGE,{"derivedFrom":sQuery(id+"F0.wireOp",EDGE,"E5.15.0.2")}),1.0]])]});
            var Q87;
            Q87=makeQuery(id+"F0.imprint","IMPRINT",FACE,{"disambiguationData":[TD([[makeQuery(id+"F0.imprint","IMPRINT",EDGE,{"derivedFrom":sQuery(id+"F0.wireOp",EDGE,"E5.16.0.2")}),1.0]])]});
            var Q88;
            Q88=makeQuery(id+"F0.imprint","IMPRINT",FACE,{"disambiguationData":[TD([[makeQuery(id+"F0.imprint","IMPRINT",EDGE,{"derivedFrom":sQuery(id+"F0.wireOp",EDGE,"E5.17.0.2")}),1.0]])]});
            var Q89;
            Q89=makeQuery(id+"F0.imprint","IMPRINT",FACE,{"disambiguationData":[TD([[makeQuery(id+"F0.imprint","IMPRINT",EDGE,{"derivedFrom":sQuery(id+"F0.wireOp",EDGE,"E5.18.0.2")}),1.0]])]});
            var Q90;
            Q90=makeQuery(id+"F0.imprint","IMPRINT",FACE,{"disambiguationData":[TD([[makeQuery(id+"F0.imprint","IMPRINT",EDGE,{"derivedFrom":sQuery(id+"F0.wireOp",EDGE,"E5.19.0.2")}),1.0]])]});
            var Q91;
            Q91=makeQuery(id+"F0.imprint","IMPRINT",FACE,{"disambiguationData":[TD([[makeQuery(id+"F0.imprint","IMPRINT",EDGE,{"derivedFrom":sQuery(id+"F0.wireOp",EDGE,"E5.19.0.3")}),1.0]])]});
            var Q92;
            Q92=makeQuery(id+"F0.imprint","IMPRINT",FACE,{"disambiguationData":[TD([[makeQuery(id+"F0.imprint","IMPRINT",EDGE,{"derivedFrom":sQuery(id+"F0.wireOp",EDGE,"E5.18.0.3")}),1.0]])]});
            var Q93;
            Q93=makeQuery(id+"F0.imprint","IMPRINT",FACE,{"disambiguationData":[TD([[makeQuery(id+"F0.imprint","IMPRINT",EDGE,{"derivedFrom":sQuery(id+"F0.wireOp",EDGE,"E5.17.0.3")}),1.0]])]});
            var Q94;
            Q94=makeQuery(id+"F0.imprint","IMPRINT",FACE,{"disambiguationData":[TD([[makeQuery(id+"F0.imprint","IMPRINT",EDGE,{"derivedFrom":sQuery(id+"F0.wireOp",EDGE,"E5.16.0.3")}),1.0]])]});
            var Q95;
            Q95=makeQuery(id+"F0.imprint","IMPRINT",FACE,{"disambiguationData":[TD([[makeQuery(id+"F0.imprint","IMPRINT",EDGE,{"derivedFrom":sQuery(id+"F0.wireOp",EDGE,"E5.15.0.3")}),1.0]])]});
            var Q96;
            Q96=makeQuery(id+"F0.imprint","IMPRINT",FACE,{"disambiguationData":[TD([[makeQuery(id+"F0.imprint","IMPRINT",EDGE,{"derivedFrom":sQuery(id+"F0.wireOp",EDGE,"E5.14.0.3")}),1.0]])]});
            var Q97;
            Q97=makeQuery(id+"F0.imprint","IMPRINT",FACE,{"disambiguationData":[TD([[makeQuery(id+"F0.imprint","IMPRINT",EDGE,{"derivedFrom":sQuery(id+"F0.wireOp",EDGE,"E5.13.0.3")}),1.0]])]});
            var Q98;
            Q98=makeQuery(id+"F0.imprint","IMPRINT",FACE,{"disambiguationData":[TD([[makeQuery(id+"F0.imprint","IMPRINT",EDGE,{"derivedFrom":sQuery(id+"F0.wireOp",EDGE,"E5.12.0.3")}),1.0]])]});
            var Q99;
            Q99=makeQuery(id+"F0.imprint","IMPRINT",FACE,{"disambiguationData":[TD([[makeQuery(id+"F0.imprint","IMPRINT",EDGE,{"derivedFrom":sQuery(id+"F0.wireOp",EDGE,"E5.11.0.3")}),1.0]])]});
            var Q100;
            Q100=makeQuery(id+"F0.imprint","IMPRINT",FACE,{"disambiguationData":[TD([[makeQuery(id+"F0.imprint","IMPRINT",EDGE,{"derivedFrom":sQuery(id+"F0.wireOp",EDGE,"E5.10.0.3")}),1.0]])]});
            var Q101;
            Q101=makeQuery(id+"F0.imprint","IMPRINT",FACE,{"disambiguationData":[TD([[makeQuery(id+"F0.imprint","IMPRINT",EDGE,{"derivedFrom":sQuery(id+"F0.wireOp",EDGE,"E5.9.0.3")}),1.0]])]});
            var Q102;
            Q102=makeQuery(id+"F0.imprint","IMPRINT",FACE,{"disambiguationData":[TD([[makeQuery(id+"F0.imprint","IMPRINT",EDGE,{"derivedFrom":sQuery(id+"F0.wireOp",EDGE,"E5.8.0.3")}),1.0]])]});
            var Q103;
            Q103=makeQuery(id+"F0.imprint","IMPRINT",FACE,{"disambiguationData":[TD([[makeQuery(id+"F0.imprint","IMPRINT",EDGE,{"derivedFrom":sQuery(id+"F0.wireOp",EDGE,"E5.7.0.3")}),1.0]])]});
            var Q104;
            Q104=makeQuery(id+"F0.imprint","IMPRINT",FACE,{"disambiguationData":[TD([[makeQuery(id+"F0.imprint","IMPRINT",EDGE,{"derivedFrom":sQuery(id+"F0.wireOp",EDGE,"E5.6.0.3")}),1.0]])]});
            var Q105;
            Q105=makeQuery(id+"F0.imprint","IMPRINT",FACE,{"disambiguationData":[TD([[makeQuery(id+"F0.imprint","IMPRINT",EDGE,{"derivedFrom":sQuery(id+"F0.wireOp",EDGE,"E5.5.0.3")}),1.0]])]});
            var Q106;
            Q106=makeQuery(id+"F0.imprint","IMPRINT",FACE,{"disambiguationData":[TD([[makeQuery(id+"F0.imprint","IMPRINT",EDGE,{"derivedFrom":sQuery(id+"F0.wireOp",EDGE,"E5.4.0.3")}),1.0]])]});
            var Q107;
            Q107=makeQuery(id+"F0.imprint","IMPRINT",FACE,{"disambiguationData":[TD([[makeQuery(id+"F0.imprint","IMPRINT",EDGE,{"derivedFrom":sQuery(id+"F0.wireOp",EDGE,"E5.3.0.3")}),1.0]])]});
            var Q108;
            Q108=makeQuery(id+"F0.imprint","IMPRINT",FACE,{"disambiguationData":[TD([[makeQuery(id+"F0.imprint","IMPRINT",EDGE,{"derivedFrom":sQuery(id+"F0.wireOp",EDGE,"E5.2.0.3")}),1.0]])]});
            var Q109;
            Q109=makeQuery(id+"F0.imprint","IMPRINT",FACE,{"disambiguationData":[TD([[makeQuery(id+"F0.imprint","IMPRINT",EDGE,{"derivedFrom":sQuery(id+"F0.wireOp",EDGE,"E5.1.0.3")}),1.0]])]});
            var Q110;
            Q110=makeQuery(id+"F0.imprint","IMPRINT",FACE,{"disambiguationData":[TD([[makeQuery(id+"F0.imprint","IMPRINT",EDGE,{"derivedFrom":sQuery(id+"F0.wireOp",EDGE,"E4.4.0.0")}),1.0]])]});
            var Q111;
            Q111=makeQuery(id+"F0.imprint","IMPRINT",FACE,{"disambiguationData":[TD([[makeQuery(id+"F0.imprint","IMPRINT",EDGE,{"derivedFrom":sQuery(id+"F0.wireOp",EDGE,"E16.1.0.0")}),1.0]])]});
            var Q112;
            Q112=makeQuery(id+"F0.imprint","IMPRINT",FACE,{"disambiguationData":[TD([[makeQuery(id+"F0.imprint","IMPRINT",EDGE,{"derivedFrom":sQuery(id+"F0.wireOp",EDGE,"E16.2.0.0")}),1.0]])]});
            var Q113;
            Q113=makeQuery(id+"F0.imprint","IMPRINT",FACE,{"disambiguationData":[TD([[makeQuery(id+"F0.imprint","IMPRINT",EDGE,{"derivedFrom":sQuery(id+"F0.wireOp",EDGE,"E16.3.0.0")}),1.0]])]});
            var Q114;
            Q114=makeQuery(id+"F0.imprint","IMPRINT",FACE,{"disambiguationData":[TD([[makeQuery(id+"F0.imprint","IMPRINT",EDGE,{"derivedFrom":sQuery(id+"F0.wireOp",EDGE,"E16.4.0.0")}),1.0]])]});
            var Q115;
            Q115=makeQuery(id+"F0.imprint","IMPRINT",FACE,{"disambiguationData":[TD([[makeQuery(id+"F0.imprint","IMPRINT",EDGE,{"derivedFrom":sQuery(id+"F0.wireOp",EDGE,"E16.5.0.0")}),1.0]])]});
            var Q116;
            Q116=makeQuery(id+"F0.imprint","IMPRINT",FACE,{"disambiguationData":[TD([[makeQuery(id+"F0.imprint","IMPRINT",EDGE,{"derivedFrom":sQuery(id+"F0.wireOp",EDGE,"E15.5.0.0")}),1.0]])]});
            var Q117;
            Q117=makeQuery(id+"F0.imprint","IMPRINT",FACE,{"disambiguationData":[TD([[makeQuery(id+"F0.imprint","IMPRINT",EDGE,{"derivedFrom":sQuery(id+"F0.wireOp",EDGE,"E15.4.0.0")}),1.0]])]});
            var Q118;
            Q118=makeQuery(id+"F0.imprint","IMPRINT",FACE,{"disambiguationData":[TD([[makeQuery(id+"F0.imprint","IMPRINT",EDGE,{"derivedFrom":sQuery(id+"F0.wireOp",EDGE,"E15.3.0.0")}),1.0]])]});
            var Q119;
            Q119=makeQuery(id+"F0.imprint","IMPRINT",FACE,{"disambiguationData":[TD([[makeQuery(id+"F0.imprint","IMPRINT",EDGE,{"derivedFrom":sQuery(id+"F0.wireOp",EDGE,"E15.2.0.0")}),1.0]])]});
            var Q120;
            Q120=makeQuery(id+"F0.imprint","IMPRINT",FACE,{"disambiguationData":[TD([[makeQuery(id+"F0.imprint","IMPRINT",EDGE,{"derivedFrom":sQuery(id+"F0.wireOp",EDGE,"E15.1.0.0")}),1.0]])]});
            var Q121;
            Q121=makeQuery(id+"F0.imprint","IMPRINT",FACE,{"disambiguationData":[TD([[makeQuery(id+"F0.imprint","IMPRINT",EDGE,{"derivedFrom":sQuery(id+"F0.wireOp",EDGE,"E4.5.0.0")}),1.0]])]});
            var Q122;
            Q122=makeQuery(id+"F0.imprint","IMPRINT",FACE,{"disambiguationData":[TD([[makeQuery(id+"F0.imprint","IMPRINT",EDGE,{"derivedFrom":sQuery(id+"F0.wireOp",EDGE,"E5.1.0.4")}),1.0]])]});
            var Q123;
            Q123=makeQuery(id+"F0.imprint","IMPRINT",FACE,{"disambiguationData":[TD([[makeQuery(id+"F0.imprint","IMPRINT",EDGE,{"derivedFrom":sQuery(id+"F0.wireOp",EDGE,"E5.2.0.4")}),1.0]])]});
            var Q124;
            Q124=makeQuery(id+"F0.imprint","IMPRINT",FACE,{"disambiguationData":[TD([[makeQuery(id+"F0.imprint","IMPRINT",EDGE,{"derivedFrom":sQuery(id+"F0.wireOp",EDGE,"E5.3.0.4")}),1.0]])]});
            var Q125;
            Q125=makeQuery(id+"F0.imprint","IMPRINT",FACE,{"disambiguationData":[TD([[makeQuery(id+"F0.imprint","IMPRINT",EDGE,{"derivedFrom":sQuery(id+"F0.wireOp",EDGE,"E5.4.0.4")}),1.0]])]});
            var Q126;
            Q126=makeQuery(id+"F0.imprint","IMPRINT",FACE,{"disambiguationData":[TD([[makeQuery(id+"F0.imprint","IMPRINT",EDGE,{"derivedFrom":sQuery(id+"F0.wireOp",EDGE,"E5.5.0.4")}),1.0]])]});
            var Q127;
            Q127=makeQuery(id+"F0.imprint","IMPRINT",FACE,{"disambiguationData":[TD([[makeQuery(id+"F0.imprint","IMPRINT",EDGE,{"derivedFrom":sQuery(id+"F0.wireOp",EDGE,"E5.6.0.4")}),1.0]])]});
            var Q128;
            Q128=makeQuery(id+"F0.imprint","IMPRINT",FACE,{"disambiguationData":[TD([[makeQuery(id+"F0.imprint","IMPRINT",EDGE,{"derivedFrom":sQuery(id+"F0.wireOp",EDGE,"E5.7.0.4")}),1.0]])]});
            var Q129;
            Q129=makeQuery(id+"F0.imprint","IMPRINT",FACE,{"disambiguationData":[TD([[makeQuery(id+"F0.imprint","IMPRINT",EDGE,{"derivedFrom":sQuery(id+"F0.wireOp",EDGE,"E5.8.0.4")}),1.0]])]});
            var Q130;
            Q130=makeQuery(id+"F0.imprint","IMPRINT",FACE,{"disambiguationData":[TD([[makeQuery(id+"F0.imprint","IMPRINT",EDGE,{"derivedFrom":sQuery(id+"F0.wireOp",EDGE,"E5.9.0.4")}),1.0]])]});
            var Q131;
            Q131=makeQuery(id+"F0.imprint","IMPRINT",FACE,{"disambiguationData":[TD([[makeQuery(id+"F0.imprint","IMPRINT",EDGE,{"derivedFrom":sQuery(id+"F0.wireOp",EDGE,"E5.10.0.4")}),1.0]])]});
            var Q132;
            Q132=makeQuery(id+"F0.imprint","IMPRINT",FACE,{"disambiguationData":[TD([[makeQuery(id+"F0.imprint","IMPRINT",EDGE,{"derivedFrom":sQuery(id+"F0.wireOp",EDGE,"E5.11.0.4")}),1.0]])]});
            var Q133;
            Q133=makeQuery(id+"F0.imprint","IMPRINT",FACE,{"disambiguationData":[TD([[makeQuery(id+"F0.imprint","IMPRINT",EDGE,{"derivedFrom":sQuery(id+"F0.wireOp",EDGE,"E5.12.0.4")}),1.0]])]});
            var Q134;
            Q134=makeQuery(id+"F0.imprint","IMPRINT",FACE,{"disambiguationData":[TD([[makeQuery(id+"F0.imprint","IMPRINT",EDGE,{"derivedFrom":sQuery(id+"F0.wireOp",EDGE,"E5.13.0.4")}),1.0]])]});
            var Q135;
            Q135=makeQuery(id+"F0.imprint","IMPRINT",FACE,{"disambiguationData":[TD([[makeQuery(id+"F0.imprint","IMPRINT",EDGE,{"derivedFrom":sQuery(id+"F0.wireOp",EDGE,"E5.14.0.4")}),1.0]])]});
            var Q136;
            Q136=makeQuery(id+"F0.imprint","IMPRINT",FACE,{"disambiguationData":[TD([[makeQuery(id+"F0.imprint","IMPRINT",EDGE,{"derivedFrom":sQuery(id+"F0.wireOp",EDGE,"E5.15.0.4")}),1.0]])]});
            var Q137;
            Q137=makeQuery(id+"F0.imprint","IMPRINT",FACE,{"disambiguationData":[TD([[makeQuery(id+"F0.imprint","IMPRINT",EDGE,{"derivedFrom":sQuery(id+"F0.wireOp",EDGE,"E5.16.0.4")}),1.0]])]});
            var Q138;
            Q138=makeQuery(id+"F0.imprint","IMPRINT",FACE,{"disambiguationData":[TD([[makeQuery(id+"F0.imprint","IMPRINT",EDGE,{"derivedFrom":sQuery(id+"F0.wireOp",EDGE,"E5.17.0.4")}),1.0]])]});
            var Q139;
            Q139=makeQuery(id+"F0.imprint","IMPRINT",FACE,{"disambiguationData":[TD([[makeQuery(id+"F0.imprint","IMPRINT",EDGE,{"derivedFrom":sQuery(id+"F0.wireOp",EDGE,"E5.18.0.4")}),1.0]])]});
            var Q140;
            Q140=makeQuery(id+"F0.imprint","IMPRINT",FACE,{"disambiguationData":[TD([[makeQuery(id+"F0.imprint","IMPRINT",EDGE,{"derivedFrom":sQuery(id+"F0.wireOp",EDGE,"E5.19.0.4")}),1.0]])]});
            extrude(context, id + "F2", {"entities" : qUnion([Q0, Q1, Q2, Q3, Q4, Q5, Q6, Q7, Q8, Q9, Q10, Q11, Q12, Q13, Q14, Q15, Q16, Q17, Q18, Q19, Q20, Q21, Q22, Q23, Q24, Q25, Q26, Q27, Q28, Q29, Q30, Q31, Q32, Q33, Q34, Q35, Q36, Q37, Q38, Q39, Q40, Q41, Q42, Q43, Q44, Q45, Q46, Q47, Q48, Q49, Q50, Q51, Q52, Q53, Q54, Q55, Q56, Q57, Q58, Q59, Q60, Q61, Q62, Q63, Q64, Q65, Q66, Q67, Q68, Q69, Q70, Q71, Q72, Q73, Q74, Q75, Q76, Q77, Q78, Q79, Q80, Q81, Q82, Q83, Q84, Q85, Q86, Q87, Q88, Q89, Q90, Q91, Q92, Q93, Q94, Q95, Q96, Q97, Q98, Q99, Q100, Q101, Q102, Q103, Q104, Q105, Q106, Q107, Q108, Q109, Q110, Q111, Q112, Q113, Q114, Q115, Q116, Q117, Q118, Q119, Q120, Q121, Q122, Q123, Q124, Q125, Q126, Q127, Q128, Q129, Q130, Q131, Q132, Q133, Q134, Q135, Q136, Q137, Q138, Q139, Q140]), "depth" : 3 * mm});
        }
    });
